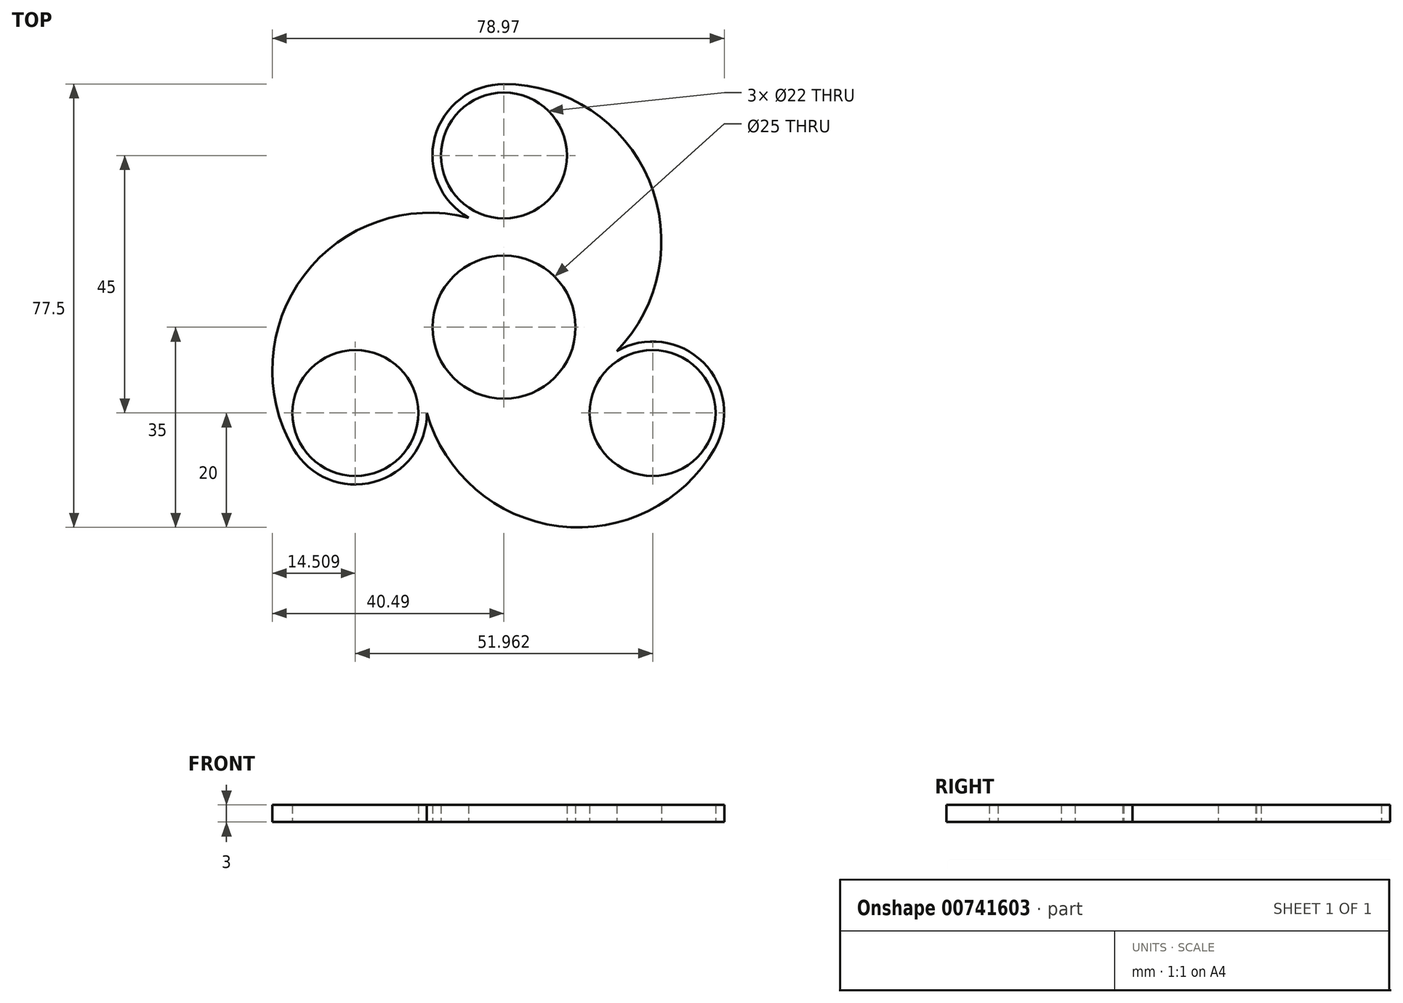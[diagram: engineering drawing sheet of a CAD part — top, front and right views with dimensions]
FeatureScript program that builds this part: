
annotation { "Feature Type Name" : "Feature", "Feature Type Description" : "" }
export const myFeature = defineFeature(function(context is Context, id is Id, definition is map)
    precondition{}
    {
        {
            var Q0;
            Q0=qCreatedBy(makeId("Top.planeOp"),FACE);
            var sketch = newSketch(context, id + "F0", { "sketchPlane" : qUnion([Q0])});
            skCircle(sketch, "E0", {"center": v(0, 0) * mm, "radius": 11 * mm});
            skArc(sketch, "E1", {"start": v(-13.48, -14.95) * mm, "mid": v(9.57, -34.79) * mm, "end": v(36.8, -21.25) * mm});
            skCircle(sketch, "E2", {"center": v(25.98, -15) * mm, "radius": 11 * mm});
            skArc(sketch, "E3", {"start": v(36.8, -21.25) * mm, "mid": v(34.8, -6.14) * mm, "end": v(19.69, -4.2) * mm});
            skCircle(sketch, "E4.1.0", {"center": v(0, 0) * mm, "radius": 12.5 * mm});
            skArc(sketch, "E4.1.2", {"start": v(0, 42.5) * mm, "mid": v(-12.08, 33.21) * mm, "end": v(-6.2, 19.15) * mm});
            skCircle(sketch, "E4.1.3", {"center": v(0, 30) * mm, "radius": 11 * mm});
            skArc(sketch, "E4.1.4", {"start": v(19.69, -4.2) * mm, "mid": v(25.34, 25.68) * mm, "end": v(0, 42.5) * mm});
            skCircle(sketch, "E4.2.0", {"center": v(0, 0) * mm, "radius": 12.5 * mm});
            skArc(sketch, "E4.2.2", {"start": v(-36.8, -21.25) * mm, "mid": v(-22.72, -27.07) * mm, "end": v(-13.48, -14.95) * mm});
            skCircle(sketch, "E4.2.3", {"center": v(-25.98, -15) * mm, "radius": 11 * mm});
            skPoint(sketch, "E5.orphan", {"position": v(0, -12.5) * mm});
            skArc(sketch, "E6.trimOffspring", {"start": v(-6.2, 19.15) * mm, "mid": v(-34.91, 9.1) * mm, "end": v(-36.8, -21.25) * mm});
            skPoint(sketch, "E7.orphan", {"position": v(-10.83, 6.25) * mm});
            skSolve(sketch);
        }
        {
            var Q0;
            Q0 = qSketchRegion(id + "F0", true);
            extrude(context, id + "F1", {"entities" : qUnion([Q0]), "depth" : 3 * mm, "offsetDistance" : 25 * mm});
        }
    });
